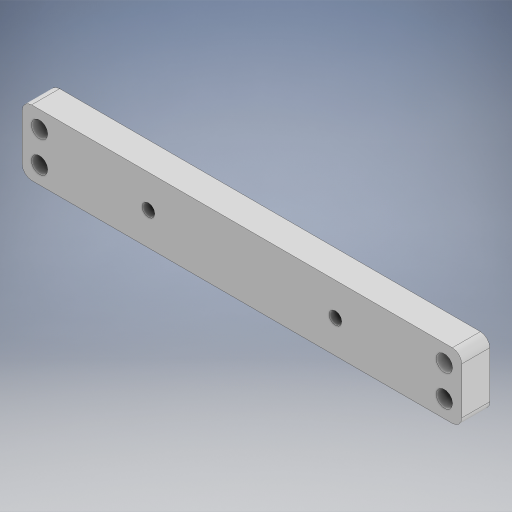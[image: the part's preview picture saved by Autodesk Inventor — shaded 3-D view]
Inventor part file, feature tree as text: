
AUTODESK INVENTOR PART (.ipt)
format: ipt  version: 2024 (Build 280153000, 153)  size: 349,184 bytes
history: native  units: mm
features: other x5, sketch x5, projected_geometry x5, reference x4, extrude x3, hole x2, fillet x1
ambient origin geometry x8: Origin, YZ Plane, XZ Plane, XY Plane, X Axis, Y Axis, Z Axis, Center Point
bodies: Body1 (feature_tree)
feature tree (25):
  other  "솔리드1"
  other  "작업 평면1"
  extrude  "돌출1"  Depth=0.3mm
  extrude  "돌출2"  Depth=4.0mm
  hole  "구멍1"  [1 undecoded]
  fillet  "모깎기1"  Radius=3.0mm
  extrude  "돌출3"  Depth=2.0mm
  hole  "구멍2"  [1 undecoded]
  sketch  "스케치1"
  reference  "참조1"
  reference  "참조2"
  sketch  "스케치2"
  projected_geometry  "투영된 루프1"
  reference  "참조3"
  reference  "참조4"
  sketch  "스케치3"
  projected_geometry  "투영된 루프2"
  sketch  "스케치4"
  projected_geometry  "투영된 루프3"
  projected_geometry  "투영된 루프4"
  sketch  "스케치5"
  projected_geometry  "투영된 루프5"
  other  "<userpath>\Desktop\ZIG\조립품1.iam"
  other  "조립품1.iam"
  other  "head:1"
note: 2 required parameter values undecoded (feature->parameter linkage not recoverable at this tier; creation-order binding heuristic only, values carry confidence <= 0.55)
